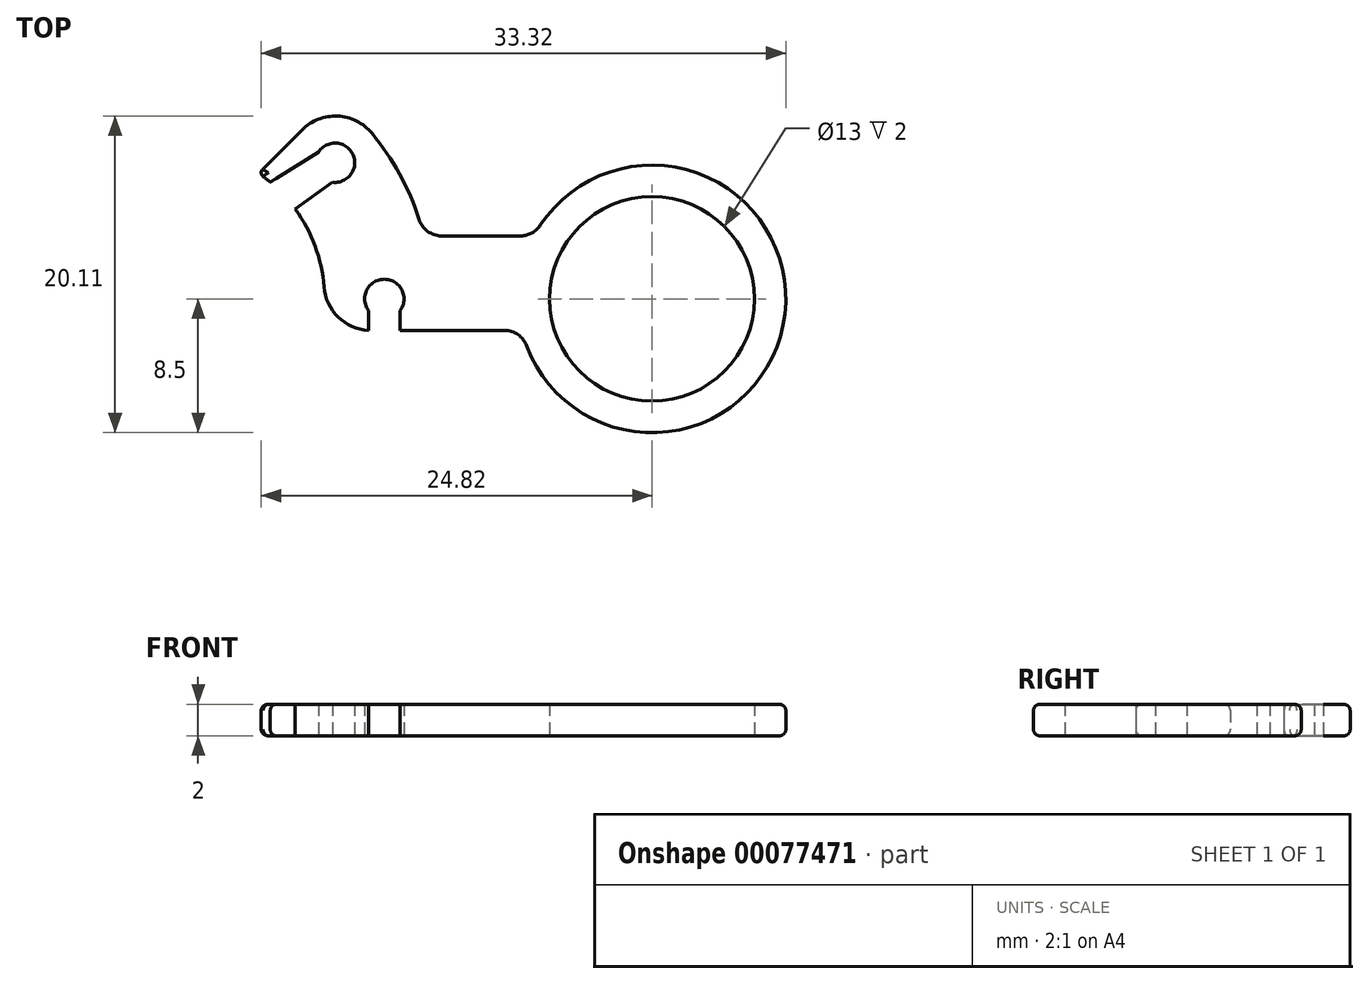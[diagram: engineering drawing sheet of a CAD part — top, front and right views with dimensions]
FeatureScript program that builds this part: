
annotation { "Feature Type Name" : "Feature", "Feature Type Description" : "" }
export const myFeature = defineFeature(function(context is Context, id is Id, definition is map)
    precondition{}
    {
        {
            var Q0;
            Q0=qCreatedBy(makeId("Top.planeOp"),FACE);
            var sketch = newSketch(context, id + "F0", { "sketchPlane" : qUnion([Q0])});
            skCircle(sketch, "E0", {"center": v(0, 0) * mm, "radius": 13.5 * mm, "construction": true});
            skCircle(sketch, "E1", {"center": v(13.5, 0) * mm, "radius": 9.2 * mm, "construction": true});
            skLineSegment(sketch, "E2", {"start": v(10.37, 8.65) * mm, "end": v(-2.46, 0) * mm, "construction": true});
            skArc(sketch, "E3", {"start": v(9.67, 0.76) * mm, "mid": v(9.1, 3.36) * mm, "end": v(7.85, 5.7) * mm});
            skArc(sketch, "E4", {"start": v(15.71, 5.04) * mm, "mid": v(14.47, 7.93) * mm, "end": v(12.7, 10.53) * mm});
            skCircle(sketch, "E5", {"center": v(30.5, 0) * mm, "radius": 6.5 * mm});
            skArc(sketch, "E6", {"start": v(22.54, -2.98) * mm, "mid": v(38.95, -0.95) * mm, "end": v(23.4, 4.68) * mm});
            skLineSegment(sketch, "E7", {"start": v(12.5, -2) * mm, "end": v(12.66, -2) * mm});
            skLineSegment(sketch, "E8", {"start": v(5.77, 8.23) * mm, "end": v(8.28, 10.73) * mm});
            skArc(sketch, "E9", {"start": v(10.2, 7.41) * mm, "mid": v(11.5, 9.17) * mm, "end": v(9.32, 9.33) * mm});
            skArc(sketch, "E10", {"start": v(14.5, -0.75) * mm, "mid": v(13.5, 1.25) * mm, "end": v(12.5, -0.75) * mm});
            skLineSegment(sketch, "E11", {"start": v(12.5, -0.75) * mm, "end": v(12.5, -2) * mm});
            skLineSegment(sketch, "E12", {"start": v(14.5, -0.75) * mm, "end": v(14.5, -2) * mm});
            skLineSegment(sketch, "E13.trimOffspring", {"start": v(14.5, -2) * mm, "end": v(21.13, -2) * mm});
            skLineSegment(sketch, "E14", {"start": v(17.14, 4) * mm, "end": v(22.15, 4) * mm});
            skLineSegment(sketch, "E15", {"start": v(0, 0) * mm, "end": v(10.2, 7.41) * mm});
            skLineSegment(sketch, "E16", {"start": v(9.32, 9.33) * mm, "end": v(6.35, 7.33) * mm, "construction": true});
            skLineSegment(sketch, "E17", {"start": v(9.32, 9.33) * mm, "end": v(6.25, 7.42) * mm});
            skArc(sketch, "E18.trimOffspring", {"start": v(6.25, 7.42) * mm, "mid": v(6.03, 7.6) * mm, "end": v(5.8, 7.77) * mm});
            skPoint(sketch, "E19.visualSharp", {"position": v(10.37, 12.83) * mm});
            skArc(sketch, "E19.filletArc", {"start": v(12.7, 10.53) * mm, "mid": v(10.54, 11.6) * mm, "end": v(8.28, 10.73) * mm});
            skPoint(sketch, "E20.visualSharp", {"position": v(9.5, -2) * mm});
            skArc(sketch, "E20.filletArc", {"start": v(9.67, 0.76) * mm, "mid": v(10.62, -1.2) * mm, "end": v(12.66, -2) * mm});
            skPoint(sketch, "E21.visualSharp", {"position": v(23, 4) * mm});
            skArc(sketch, "E21.filletArc", {"start": v(22.15, 4) * mm, "mid": v(22.86, 4.18) * mm, "end": v(23.4, 4.67) * mm});
            skPoint(sketch, "E22.visualSharp", {"position": v(22.24, -2) * mm});
            skArc(sketch, "E22.filletArc", {"start": v(22.54, -2.97) * mm, "mid": v(21.99, -2.27) * mm, "end": v(21.13, -2) * mm});
            skPoint(sketch, "E23.visualSharp", {"position": v(16, 4) * mm});
            skArc(sketch, "E23.filletArc", {"start": v(15.71, 5.04) * mm, "mid": v(16.26, 4.29) * mm, "end": v(17.14, 4) * mm});
            skPoint(sketch, "E24.visualSharp", {"position": v(5.52, 7.98) * mm});
            skArc(sketch, "E24.filletArc", {"start": v(5.77, 8.23) * mm, "mid": v(5.68, 8) * mm, "end": v(5.8, 7.77) * mm});
            skSolve(sketch);
        }
        {
            var Q0;
            {var subQ3=sQuery(id+"F0.wireOp",EDGE,"E7");var subQ6=sQuery(id+"F0.wireOp",EDGE,"E3");Q0=qUnion([makeQuery(id+"F0.imprint","IMPRINT",FACE,{"disambiguationData":[TD([[makeQuery(id+"F0.imprint","IMPRINT",EDGE,{"derivedFrom":subQ3}),1.0]])]}),makeQuery(id+"F0.imprint","IMPRINT",FACE,{"disambiguationData":[TD([[makeQuery(id+"F0.imprint","IMPRINT",EDGE,{"derivedFrom":subQ6}),-1.0]])]})]);}
            extrude(context, id + "F1", {"entities" : qUnion([Q0]), "depth" : 2 * mm});
        }
        {
            var Q0;
            Q0=makeQuery(id+"F1.opExtrude","CAP_EDGE",EDGE,{"disambiguationData":[OSD([sQuery(id+"F0.wireOp",EDGE,"E13.trimOffspring")])],"isStart":false});
            var Q1;
            Q1=makeQuery(id+"F1.opExtrude","CAP_EDGE",EDGE,{"disambiguationData":[OSD([sQuery(id+"F0.wireOp",EDGE,"E13.trimOffspring")])],"isStart":true});
            fillet(context, id + "F2", {"entities" : qUnion([Q0, Q1]), "radius" : 0.4 * mm, "tangentPropagation" : true, "allowEdgeOverflow" : false});
        }
        {
            var Q0;
            Q0=makeQuery(id+"F1.opExtrude","SWEPT_BODY",BODY,{"disambiguationData":[OSD([sQuery(id+"F0.wireOp",EDGE,"E7"),sQuery(id+"F0.wireOp",EDGE,"E11"),sQuery(id+"F0.wireOp",EDGE,"E20.filletArc")])]});
            deleteBodies(context, id + "F3", {"entities" : qUnion([Q0])});
        }
    });
